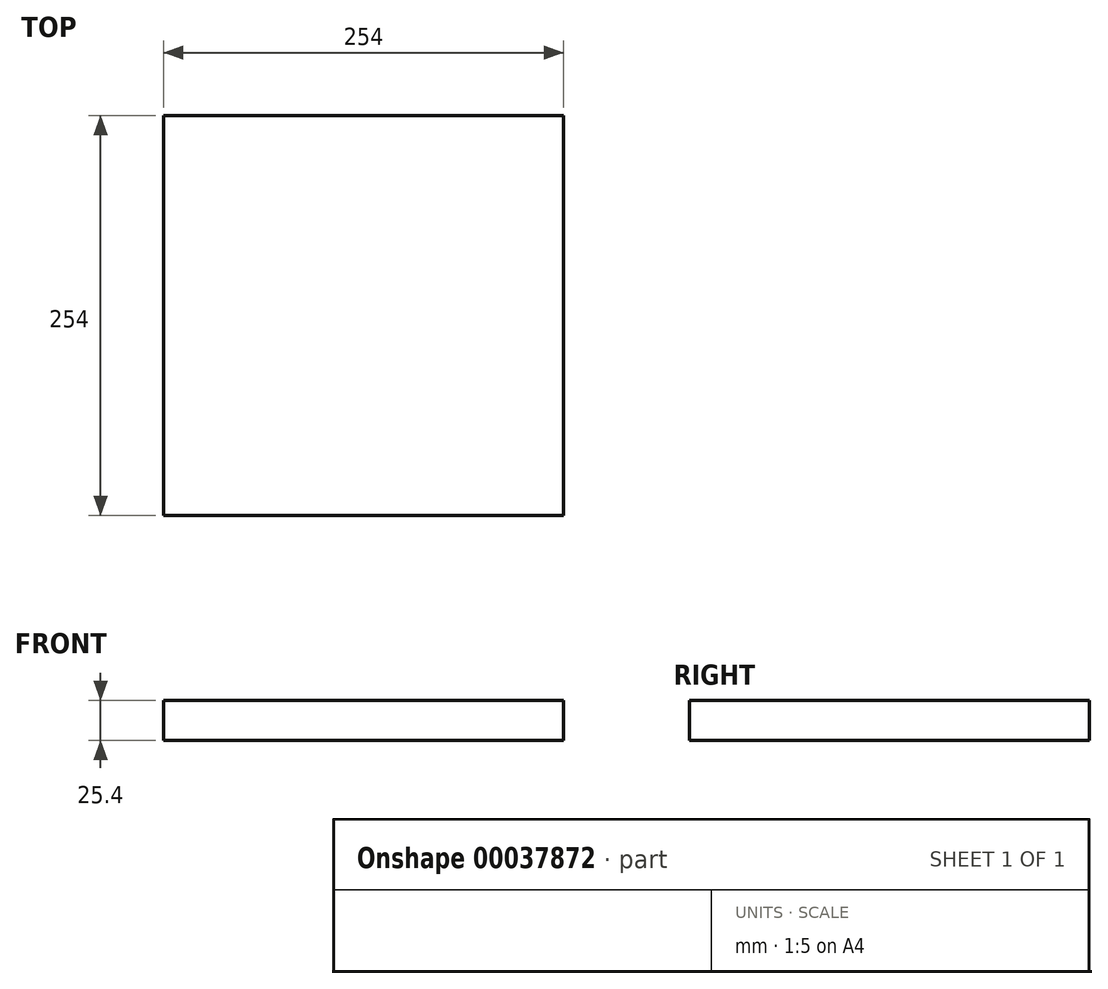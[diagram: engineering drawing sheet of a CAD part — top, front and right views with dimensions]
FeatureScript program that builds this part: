
annotation { "Feature Type Name" : "Feature", "Feature Type Description" : "" }
export const myFeature = defineFeature(function(context is Context, id is Id, definition is map)
    precondition{}
    {
        {
            var Q0;
            Q0=qCreatedBy(makeId("Top.planeOp"),FACE);
            var sketch = newSketch(context, id + "F0", { "sketchPlane" : qUnion([Q0])});
            skLineSegment(sketch, "E0.bottom", {"start": v(0, 0) * mm, "end": v(254, 0) * mm});
            skLineSegment(sketch, "E0.top", {"start": v(0, -254) * mm, "end": v(254, -254) * mm});
            skLineSegment(sketch, "E0.left", {"start": v(0, 0) * mm, "end": v(0, -254) * mm});
            skLineSegment(sketch, "E0.right", {"start": v(254, 0) * mm, "end": v(254, -254) * mm});
            skSolve(sketch);
        }
        {
            var Q0;
            Q0 = qSketchRegion(id + "F0", true);
            extrude(context, id + "F1", {"entities" : qUnion([Q0]), "depth" : 25.4 * mm});
        }
    });
